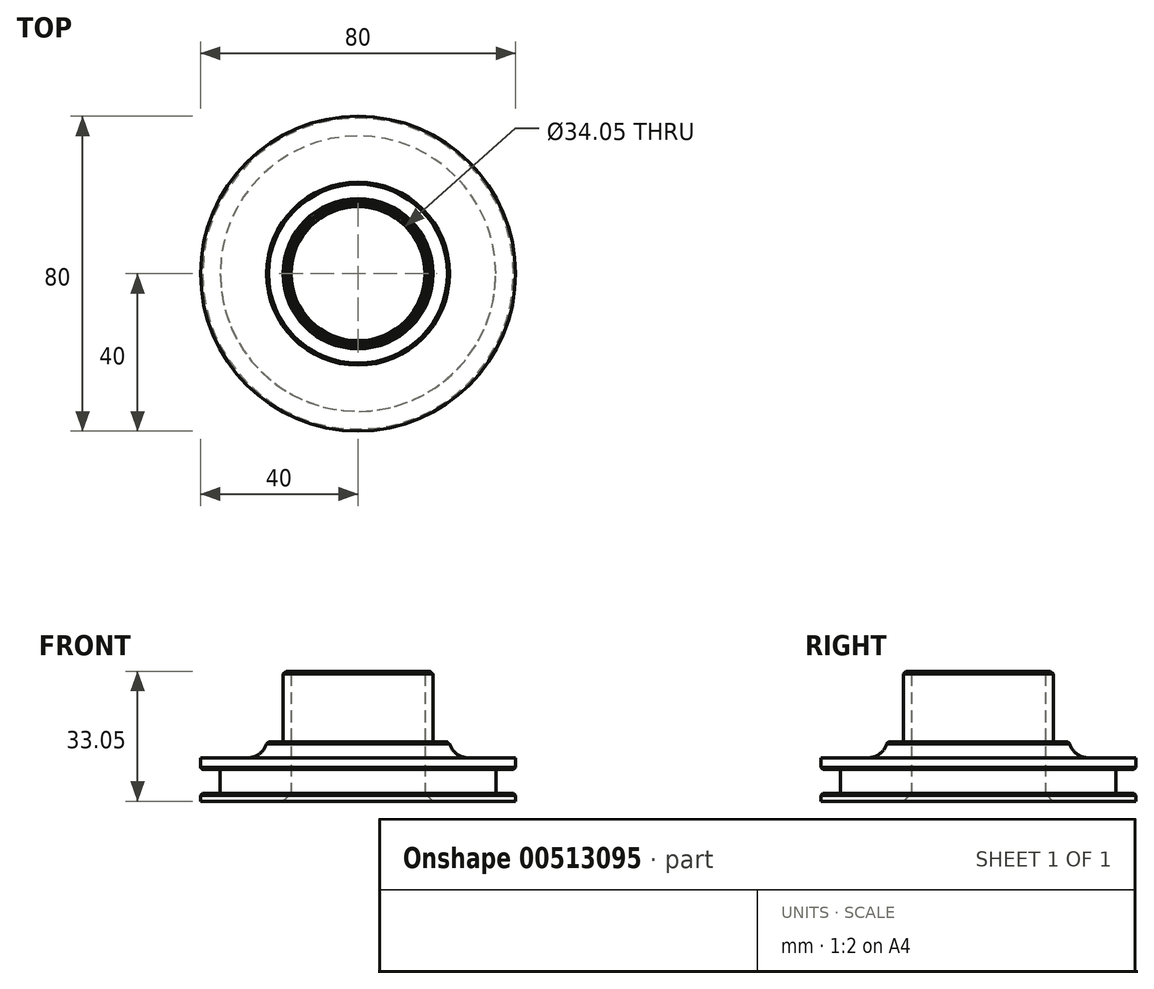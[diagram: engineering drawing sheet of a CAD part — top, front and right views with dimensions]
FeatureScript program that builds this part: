
annotation { "Feature Type Name" : "Feature", "Feature Type Description" : "" }
export const myFeature = defineFeature(function(context is Context, id is Id, definition is map)
    precondition{}
    {
        {
            var Q0;
            Q0=qCreatedBy(makeId("Front.planeOp"),FACE);
            var sketch = newSketch(context, id + "F0", { "sketchPlane" : qUnion([Q0])});
            skLineSegment(sketch, "E0", {"start": v(17.02, 0) * mm, "end": v(40, 0) * mm});
            skLineSegment(sketch, "E1", {"start": v(40, 0) * mm, "end": v(40, 2) * mm});
            skLineSegment(sketch, "E2", {"start": v(40, 2) * mm, "end": v(35, 2) * mm});
            skLineSegment(sketch, "E3", {"start": v(35, 2) * mm, "end": v(35, 8.05) * mm});
            skLineSegment(sketch, "E4", {"start": v(35, 8.05) * mm, "end": v(40, 8.05) * mm});
            skLineSegment(sketch, "E5", {"start": v(40, 8.05) * mm, "end": v(40, 11.05) * mm});
            skLineSegment(sketch, "E6", {"start": v(40, 11.05) * mm, "end": v(23.25, 11.05) * mm});
            skLineSegment(sketch, "E7", {"start": v(23.25, 11.05) * mm, "end": v(23.25, 15.05) * mm});
            skLineSegment(sketch, "E8", {"start": v(23.25, 15.05) * mm, "end": v(19.06, 15.05) * mm});
            skLineSegment(sketch, "E9", {"start": v(19.06, 15.05) * mm, "end": v(19.06, 33.05) * mm});
            skLineSegment(sketch, "E10", {"start": v(19.06, 33.05) * mm, "end": v(17.02, 33.05) * mm});
            skLineSegment(sketch, "E11", {"start": v(17.02, 33.05) * mm, "end": v(17.03, 0) * mm});
            skLineSegment(sketch, "E12", {"start": v(0, 0) * mm, "end": v(0, 27.89) * mm});
            skSolve(sketch);
        }
        {
            var Q0;
            Q0=makeQuery(id+"F0.imprint","IMPRINT",FACE,{"disambiguationData":[TD([[makeQuery(id+"F0.imprint","IMPRINT",EDGE,{"derivedFrom":sQuery(id+"F0.wireOp",EDGE,"E0")}),1.0]])]});
            var Q1;
            Q1=sQuery(id+"F0.wireOp",EDGE,"E12");
            revolve(context, id + "F1", {"entities" : qUnion([Q0]), "axis" : qUnion([Q1]), "revolveType" : RevolveType.FULL});
        }
        {
            var Q0;
            Q0=makeQuery(id+"F1.opRevolve","SWEPT_EDGE",EDGE,{"disambiguationData":[OSD([sQuery(id+"F0.wireOp",EDGE,"E0"),sQuery(id+"F0.wireOp",EDGE,"E11")])]});
            chamfer(context, id + "F2", {"entities" : qUnion([Q0]), "width" : 2 * mm, "tangentPropagation" : true});
        }
        {
            var Q0;
            Q0=makeQuery(id+"F1.opRevolve","SWEPT_EDGE",EDGE,{"disambiguationData":[OSD([sQuery(id+"F0.wireOp",EDGE,"E10"),sQuery(id+"F0.wireOp",EDGE,"E11")])]});
            var Q1;
            Q1=makeQuery(id+"F1.opRevolve","SWEPT_EDGE",EDGE,{"disambiguationData":[OSD([sQuery(id+"F0.wireOp",EDGE,"E9"),sQuery(id+"F0.wireOp",EDGE,"E10")])]});
            chamfer(context, id + "F3", {"entities" : qUnion([Q0, Q1]), "width" : 0.75 * mm, "tangentPropagation" : true});
        }
        {
            var Q0;
            Q0=makeQuery(id+"F1.opRevolve","SWEPT_EDGE",EDGE,{"disambiguationData":[OSD([sQuery(id+"F0.wireOp",EDGE,"E7"),sQuery(id+"F0.wireOp",EDGE,"E8")])]});
            var Q1;
            Q1=makeQuery(id+"F1.opRevolve","SWEPT_EDGE",EDGE,{"disambiguationData":[OSD([sQuery(id+"F0.wireOp",EDGE,"E4"),sQuery(id+"F0.wireOp",EDGE,"E5")])]});
            var Q2;
            Q2=makeQuery(id+"F1.opRevolve","SWEPT_EDGE",EDGE,{"disambiguationData":[OSD([sQuery(id+"F0.wireOp",EDGE,"E1"),sQuery(id+"F0.wireOp",EDGE,"E2")])]});
            chamfer(context, id + "F4", {"entities" : qUnion([Q0, Q1, Q2]), "width" : 0.5 * mm, "tangentPropagation" : true});
        }
        {
            var Q0;
            Q0=makeQuery(id+"F1.opRevolve","SWEPT_EDGE",EDGE,{"disambiguationData":[OSD([sQuery(id+"F0.wireOp",EDGE,"E3"),sQuery(id+"F0.wireOp",EDGE,"E4")])]});
            var Q1;
            Q1=makeQuery(id+"F1.opRevolve","SWEPT_EDGE",EDGE,{"disambiguationData":[OSD([sQuery(id+"F0.wireOp",EDGE,"E2"),sQuery(id+"F0.wireOp",EDGE,"E3")])]});
            var Q2;
            Q2=makeQuery(id+"F1.opRevolve","SWEPT_EDGE",EDGE,{"disambiguationData":[OSD([sQuery(id+"F0.wireOp",EDGE,"E8"),sQuery(id+"F0.wireOp",EDGE,"E9")])]});
            fillet(context, id + "F5", {"entities" : qUnion([Q0, Q1, Q2]), "radius" : 0.5 * mm, "tangentPropagation" : true, "allowEdgeOverflow" : false});
        }
        {
            var Q0;
            Q0=makeQuery(id+"F1.opRevolve","SWEPT_EDGE",EDGE,{"disambiguationData":[OSD([sQuery(id+"F0.wireOp",EDGE,"E6"),sQuery(id+"F0.wireOp",EDGE,"E7")])]});
            fillet(context, id + "F6", {"entities" : qUnion([Q0]), "radius" : 5 * mm, "tangentPropagation" : true, "allowEdgeOverflow" : false});
        }
    });
